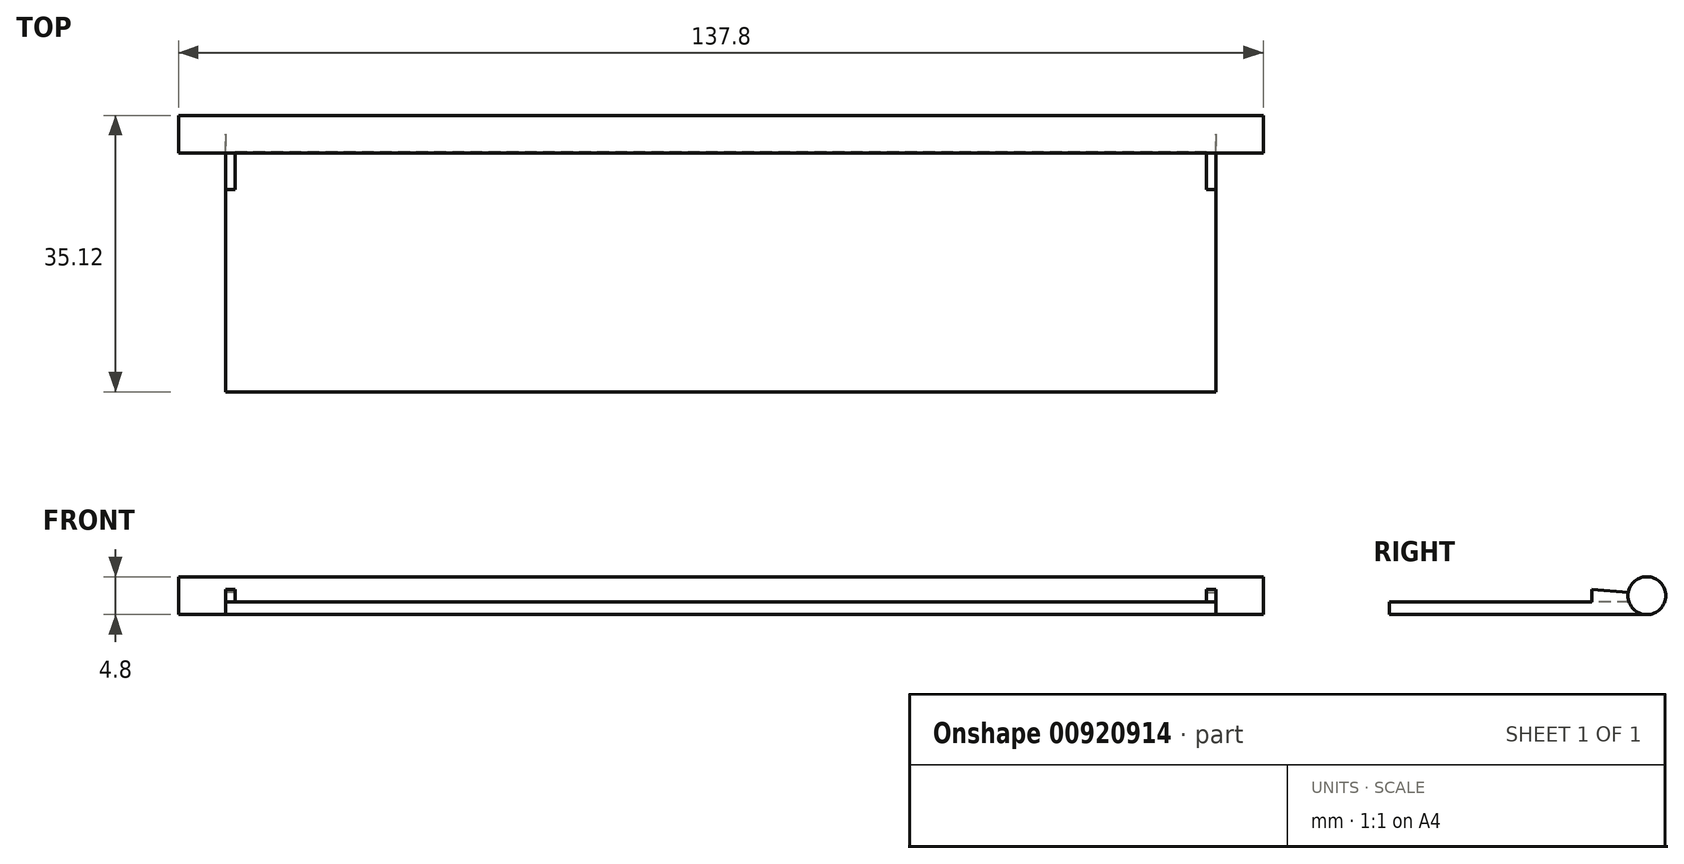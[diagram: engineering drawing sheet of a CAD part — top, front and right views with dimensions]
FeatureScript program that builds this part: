
annotation { "Feature Type Name" : "Feature", "Feature Type Description" : "" }
export const myFeature = defineFeature(function(context is Context, id is Id, definition is map)
    precondition{}
    {
        {
            var Q0;
            Q0=qCreatedBy(makeId("Top.planeOp"),FACE);
            var sketch = newSketch(context, id + "F0", { "sketchPlane" : qUnion([Q0])});
            skLineSegment(sketch, "E0", {"start": v(-68.9, 2.4) * mm, "end": v(68.9, 2.4) * mm});
            skLineSegment(sketch, "E1", {"start": v(68.9, 2.4) * mm, "end": v(68.9, 0) * mm});
            skLineSegment(sketch, "E2", {"start": v(68.9, 0) * mm, "end": v(-68.9, 0) * mm});
            skLineSegment(sketch, "E3", {"start": v(-68.9, 0) * mm, "end": v(-68.9, 2.4) * mm});
            skLineSegment(sketch, "E4", {"start": v(-75.39, 0) * mm, "end": v(0, 0) * mm, "construction": true});
            skSolve(sketch);
        }
        {
            var Q0;
            Q0=makeQuery(id+"F0.imprint","IMPRINT",FACE,{"disambiguationData":[TD([[makeQuery(id+"F0.imprint","IMPRINT",EDGE,{"derivedFrom":sQuery(id+"F0.wireOp",EDGE,"E0")}),-1.0]])]});
            var Q1;
            Q1=sQuery(id+"F0.wireOp",EDGE,"E4");
            revolve(context, id + "F1", {"surfaceOperationType" : NewSurfaceOperationType.NEW, "entities" : qUnion([Q0]), "axis" : qUnion([Q1]), "revolveType" : RevolveType.FULL});
        }
        {
            var Q0;
            Q0=qCreatedBy(makeId("Right.planeOp"),FACE);
            var sketch = newSketch(context, id + "F2", { "sketchPlane" : qUnion([Q0])});
            skLineSegment(sketch, "E5", {"start": v(0, -2.4) * mm, "end": v(-32.72, -2.4) * mm});
            skLineSegment(sketch, "E6", {"start": v(-32.72, -2.4) * mm, "end": v(-32.72, -0.8) * mm});
            skLineSegment(sketch, "E7", {"start": v(-32.72, -0.8) * mm, "end": v(0, -0.8) * mm});
            skPoint(sketch, "E8", {"position": v(2.4, 0) * mm});
            skLineSegment(sketch, "E9", {"start": v(0, -0.8) * mm, "end": v(0, -2.4) * mm});
            skLineSegment(sketch, "E10", {"start": v(0, -0.8) * mm, "end": v(0, 0.19) * mm});
            skLineSegment(sketch, "E11", {"start": v(0, 0.19) * mm, "end": v(-7, 0.8) * mm});
            skLineSegment(sketch, "E12", {"start": v(-7, 0.8) * mm, "end": v(-7, -0.8) * mm});
            skSolve(sketch);
        }
        {
            var Q0;
            Q0=makeQuery(id+"F2.imprint","IMPRINT",FACE,{"disambiguationData":[TD([[makeQuery(id+"F2.imprint","IMPRINT",EDGE,{"derivedFrom":sQuery(id+"F2.wireOp",EDGE,"E5")}),-1.0]])]});
            extrude(context, id + "F3", {"entities" : qUnion([Q0]), "operationType" : NewBodyOperationType.ADD, "endBound" : BoundingType.SYMMETRIC, "depth" : (137.8 - 12) * mm, "offsetDistance" : 25 * mm});
        }
        {
            var Q0;
            {var subQ0=sQuery(id+"F2.wireOp",EDGE,"E10");Q0=makeQuery(id+"F2.imprint","IMPRINT",FACE,{"disambiguationData":[TD([[makeQuery(id+"F2.imprint","IMPRINT",EDGE,{"derivedFrom":subQ0}),1.0]])]});}
            var Q1;
            Q1=makeQuery(id+"F3.opExtrude","CAP_FACE",FACE,{"disambiguationData":[OSD([sQuery(id+"F2.wireOp",EDGE,"E5"),sQuery(id+"F2.wireOp",EDGE,"E6"),sQuery(id+"F2.wireOp",EDGE,"E7"),sQuery(id+"F2.wireOp",EDGE,"E9")])],"isStart":true});
            var Q2;
            Q2=makeQuery(id+"F3.opExtrude","CAP_FACE",FACE,{"disambiguationData":[OSD([sQuery(id+"F2.wireOp",EDGE,"E5"),sQuery(id+"F2.wireOp",EDGE,"E6"),sQuery(id+"F2.wireOp",EDGE,"E7"),sQuery(id+"F2.wireOp",EDGE,"E9")])],"isStart":true});
            extrude(context, id + "F4", {"entities" : qUnion([Q0]), "operationType" : NewBodyOperationType.ADD, "endBound" : BoundingType.UP_TO_SURFACE, "oppositeDirection" : true, "depth" : 2 * mm, "endBoundEntityFace" : qUnion([Q1]), "offsetDistance" : 25 * mm, "hasSecondDirection" : true, "secondDirectionBound" : SecondDirectionBoundingType.UP_TO_SURFACE, "secondDirectionOppositeDirection" : true, "secondDirectionDepth" : 25 * mm, "secondDirectionBoundEntityFace" : qUnion([Q2]), "hasSecondDirectionOffset" : true, "secondDirectionOffsetDistance" : 1.2 * mm});
        }
        {
            var Q0;
            Q0=makeQuery(id+"F1.opRevolve","SWEPT_BODY",BODY,{"disambiguationData":[OSD([sQuery(id+"F0.wireOp",EDGE,"E0"),sQuery(id+"F0.wireOp",EDGE,"E1"),sQuery(id+"F0.wireOp",EDGE,"E2"),sQuery(id+"F0.wireOp",EDGE,"E3")])]});
            var Q1;
            Q1=qCreatedBy(makeId("Right.planeOp"),FACE);
            mirror(context, id + "F5", {"operationType" : NewBodyOperationType.ADD, "entities" : qUnion([Q0]), "mirrorPlane" : qUnion([Q1])});
        }
    });
